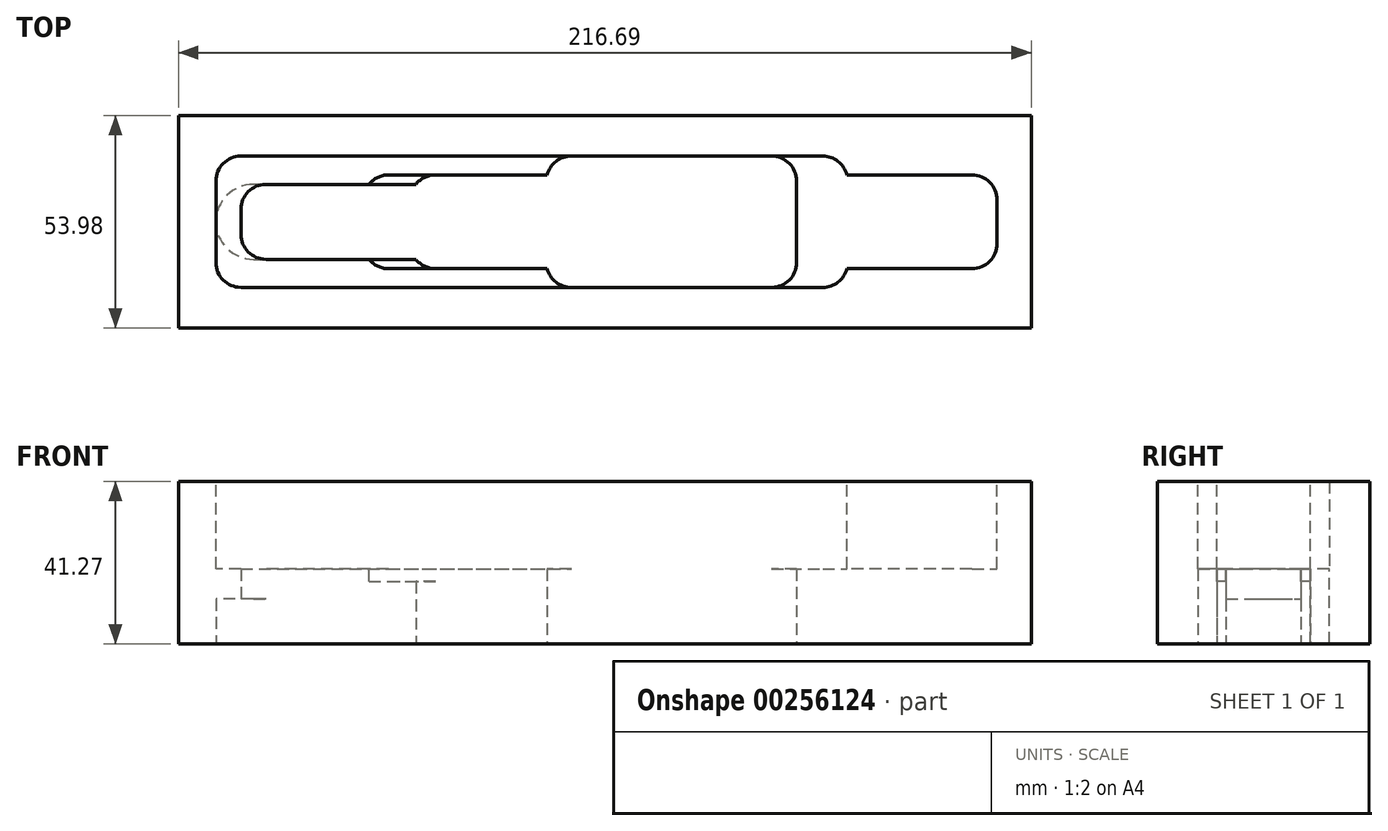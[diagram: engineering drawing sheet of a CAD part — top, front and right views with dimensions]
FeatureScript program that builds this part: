
annotation { "Feature Type Name" : "Feature", "Feature Type Description" : "" }
export const myFeature = defineFeature(function(context is Context, id is Id, definition is map)
    precondition{}
    {
        {
            var Q0;
            Q0=qCreatedBy(makeId("Top.planeOp"),FACE);
            var sketch = newSketch(context, id + "F0", { "sketchPlane" : qUnion([Q0])});
            skLineSegment(sketch, "E0.bottom", {"start": v(127, 26.99) * mm, "end": v(-127, 26.99) * mm});
            skLineSegment(sketch, "E0.top", {"start": v(127, -26.99) * mm, "end": v(-127, -26.99) * mm});
            skLineSegment(sketch, "E0.left", {"start": v(127, 26.99) * mm, "end": v(127, -26.99) * mm});
            skLineSegment(sketch, "E0.right", {"start": v(-127, 26.99) * mm, "end": v(-127, -26.99) * mm});
            skPoint(sketch, "E0.middle", {"position": v(0, 0) * mm});
            skSolve(sketch);
        }
        {
            var Q0;
            Q0 = qSketchRegion(id + "F0", true);
            extrude(context, id + "F1", {"entities" : qUnion([Q0]), "depth" : 41.27 * mm});
        }
        {
            var Q0;
            Q0=makeQuery(id+"F1.opExtrude","CAP_FACE",FACE,{"disambiguationData":[OSD([sQuery(id+"F0.wireOp",EDGE,"E0.bottom"),sQuery(id+"F0.wireOp",EDGE,"E0.top"),sQuery(id+"F0.wireOp",EDGE,"E0.left"),sQuery(id+"F0.wireOp",EDGE,"E0.right")])],"isStart":false});
            var sketch = newSketch(context, id + "F2", { "sketchPlane" : qUnion([Q0])});
            skLineSegment(sketch, "E1.bottom", {"start": v(-80.17, -16.67) * mm, "end": v(80.17, -16.67) * mm});
            skLineSegment(sketch, "E1.top", {"start": v(-80.17, 16.67) * mm, "end": v(80.17, 16.67) * mm});
            skLineSegment(sketch, "E1.left", {"start": v(-80.17, -16.67) * mm, "end": v(-80.17, 16.67) * mm});
            skPoint(sketch, "E1.middle", {"position": v(0, 0) * mm});
            skLineSegment(sketch, "E2", {"start": v(80.17, 16.67) * mm, "end": v(80.17, 11.9) * mm});
            skLineSegment(sketch, "E3", {"start": v(80.17, 11.9) * mm, "end": v(118.27, 11.9) * mm});
            skLineSegment(sketch, "E4", {"start": v(118.27, 11.9) * mm, "end": v(118.27, -11.9) * mm});
            skLineSegment(sketch, "E5", {"start": v(118.27, -11.9) * mm, "end": v(80.17, -11.9) * mm});
            skLineSegment(sketch, "E6", {"start": v(80.17, -11.9) * mm, "end": v(80.17, -16.67) * mm});
            skSolve(sketch);
        }
        {
            var Q0;
            Q0 = qSketchRegion(id + "F2", true);
            extrude(context, id + "F3", {"entities" : qUnion([Q0]), "operationType" : NewBodyOperationType.REMOVE, "oppositeDirection" : true, "depth" : 22.22 * mm});
        }
        {
            var Q0;
            Q0=makeQuery(id+"F3.boolean.opBoolean","COPY",EDGE,{"derivedFrom":makeQuery(id+"F3.opExtrude","SWEPT_EDGE",EDGE,{"disambiguationData":[OSD([sQuery(id+"F2.wireOp",EDGE,"E1.bottom"),sQuery(id+"F2.wireOp",EDGE,"E1.left")])]})});
            var Q1;
            Q1=makeQuery(id+"F3.boolean.opBoolean","COPY",EDGE,{"derivedFrom":makeQuery(id+"F3.opExtrude","SWEPT_EDGE",EDGE,{"disambiguationData":[OSD([sQuery(id+"F2.wireOp",EDGE,"E4"),sQuery(id+"F2.wireOp",EDGE,"E5")])]})});
            var Q2;
            Q2=makeQuery(id+"F3.boolean.opBoolean","COPY",EDGE,{"derivedFrom":makeQuery(id+"F3.opExtrude","SWEPT_EDGE",EDGE,{"disambiguationData":[OSD([sQuery(id+"F2.wireOp",EDGE,"E3"),sQuery(id+"F2.wireOp",EDGE,"E4")])]})});
            var Q3;
            Q3=makeQuery(id+"F3.boolean.opBoolean","COPY",EDGE,{"derivedFrom":makeQuery(id+"F3.opExtrude","SWEPT_EDGE",EDGE,{"disambiguationData":[OSD([sQuery(id+"F2.wireOp",EDGE,"E1.top"),sQuery(id+"F2.wireOp",EDGE,"E2")])]})});
            var Q4;
            Q4=makeQuery(id+"F3.boolean.opBoolean","COPY",EDGE,{"derivedFrom":makeQuery(id+"F3.opExtrude","SWEPT_EDGE",EDGE,{"disambiguationData":[OSD([sQuery(id+"F2.wireOp",EDGE,"E1.top"),sQuery(id+"F2.wireOp",EDGE,"E1.left")])]})});
            var Q5;
            Q5=makeQuery(id+"F3.boolean.opBoolean","COPY",EDGE,{"derivedFrom":makeQuery(id+"F3.opExtrude","SWEPT_EDGE",EDGE,{"disambiguationData":[OSD([sQuery(id+"F2.wireOp",EDGE,"E1.bottom"),sQuery(id+"F2.wireOp",EDGE,"E6")])]})});
            fillet(context, id + "F4", {"entities" : qUnion([Q0, Q1, Q2, Q3, Q4, Q5]), "radius" : 6.35 * mm, "tangentPropagation" : true, "allowEdgeOverflow" : false});
        }
        {
            var Q0;
            Q0=makeQuery(id+"F1.opExtrude","CAP_FACE",FACE,{"disambiguationData":[OSD([sQuery(id+"F0.wireOp",EDGE,"E0.bottom"),sQuery(id+"F0.wireOp",EDGE,"E0.top"),sQuery(id+"F0.wireOp",EDGE,"E0.left"),sQuery(id+"F0.wireOp",EDGE,"E0.right")])],"isStart":true});
            var sketch = newSketch(context, id + "F5", { "sketchPlane" : qUnion([Q0])});
            skLineSegment(sketch, "E7", {"start": v(-70.64, 9.52) * mm, "end": v(-29.37, 9.52) * mm});
            skLineSegment(sketch, "E8", {"start": v(-29.37, 9.52) * mm, "end": v(-29.37, 11.9) * mm});
            skLineSegment(sketch, "E9", {"start": v(-29.37, 11.9) * mm, "end": v(3.97, 11.9) * mm});
            skLineSegment(sketch, "E10", {"start": v(3.97, 11.9) * mm, "end": v(3.97, 16.67) * mm});
            skLineSegment(sketch, "E11", {"start": v(3.97, 16.67) * mm, "end": v(67.39, 16.67) * mm});
            skLineSegment(sketch, "E12", {"start": v(67.39, 16.67) * mm, "end": v(67.39, -16.67) * mm});
            skLineSegment(sketch, "E13", {"start": v(67.39, -16.67) * mm, "end": v(3.97, -16.67) * mm});
            skLineSegment(sketch, "E14", {"start": v(3.97, -16.67) * mm, "end": v(3.97, -11.9) * mm});
            skLineSegment(sketch, "E15", {"start": v(3.97, -11.9) * mm, "end": v(-29.37, -11.9) * mm});
            skLineSegment(sketch, "E16", {"start": v(-29.37, -11.9) * mm, "end": v(-29.37, -9.53) * mm});
            skLineSegment(sketch, "E17", {"start": v(-29.37, -9.53) * mm, "end": v(-70.64, -9.53) * mm});
            skArc(sketch, "E18", {"start": v(-70.64, 9.52) * mm, "mid": v(-80.17, 0) * mm, "end": v(-70.64, -9.53) * mm});
            skSolve(sketch);
        }
        {
            var Q0;
            Q0 = qSketchRegion(id + "F5", true);
            extrude(context, id + "F6", {"entities" : qUnion([Q0]), "operationType" : NewBodyOperationType.REMOVE, "oppositeDirection" : true, "depth" : 11.43 * mm});
        }
        {
            var Q0;
            Q0=makeQuery(id+"F1.opExtrude","CAP_FACE",FACE,{"disambiguationData":[OSD([sQuery(id+"F0.wireOp",EDGE,"E0.bottom"),sQuery(id+"F0.wireOp",EDGE,"E0.top"),sQuery(id+"F0.wireOp",EDGE,"E0.left"),sQuery(id+"F0.wireOp",EDGE,"E0.right")])],"isStart":true});
            var sketch = newSketch(context, id + "F7", { "sketchPlane" : qUnion([Q0])});
            skLineSegment(sketch, "E19", {"start": v(-70.64, 9.52) * mm, "end": v(-29.37, 9.52) * mm});
            skLineSegment(sketch, "E20", {"start": v(-29.37, 9.52) * mm, "end": v(-29.37, 11.9) * mm});
            skLineSegment(sketch, "E21", {"start": v(-29.37, 11.9) * mm, "end": v(3.97, 11.9) * mm});
            skLineSegment(sketch, "E22", {"start": v(3.97, 11.9) * mm, "end": v(3.97, 16.67) * mm});
            skLineSegment(sketch, "E23", {"start": v(3.97, 16.67) * mm, "end": v(67.39, 16.67) * mm});
            skLineSegment(sketch, "E24", {"start": v(67.39, 16.67) * mm, "end": v(67.39, -16.67) * mm});
            skLineSegment(sketch, "E25", {"start": v(67.39, -16.67) * mm, "end": v(3.97, -16.67) * mm});
            skLineSegment(sketch, "E26", {"start": v(3.97, -16.67) * mm, "end": v(3.97, -11.9) * mm});
            skLineSegment(sketch, "E27", {"start": v(3.97, -11.9) * mm, "end": v(-29.37, -11.9) * mm});
            skLineSegment(sketch, "E28", {"start": v(-29.37, -11.9) * mm, "end": v(-29.37, -9.53) * mm});
            skLineSegment(sketch, "E29", {"start": v(-29.37, -9.53) * mm, "end": v(-70.64, -9.53) * mm});
            skArc(sketch, "E30", {"start": v(-70.64, 9.52) * mm, "mid": v(-72.25, 9.39) * mm, "end": v(-73.82, 8.98) * mm});
            skArc(sketch, "E31", {"start": v(-70.64, -9.53) * mm, "mid": v(-72.25, -9.39) * mm, "end": v(-73.82, -8.98) * mm});
            skLineSegment(sketch, "E32", {"start": v(-73.82, 8.98) * mm, "end": v(-73.82, -8.98) * mm});
            skSolve(sketch);
        }
        {
            var Q0;
            Q0 = qSketchRegion(id + "F7", true);
            extrude(context, id + "F8", {"entities" : qUnion([Q0]), "operationType" : NewBodyOperationType.REMOVE, "endBound" : BoundingType.THROUGH_ALL, "oppositeDirection" : true, "depth" : 25.4 * mm});
        }
        {
            var Q0;
            Q0=makeQuery(id+"F8.boolean.opBoolean","MERGE",EDGE,{"derivedFrom":[makeQuery(id+"F6.boolean.opBoolean","COPY",EDGE,{"derivedFrom":makeQuery(id+"F6.opExtrude","SWEPT_EDGE",EDGE,{"disambiguationData":[OSD([sQuery(id+"F5.wireOp",EDGE,"E10"),sQuery(id+"F5.wireOp",EDGE,"E11")])]})}),makeQuery(id+"F8.opExtrude","SWEPT_EDGE",EDGE,{"disambiguationData":[OSD([sQuery(id+"F7.wireOp",EDGE,"E22"),sQuery(id+"F7.wireOp",EDGE,"E23")])]})]});
            var Q1;
            Q1=makeQuery(id+"F8.boolean.opBoolean","MERGE",EDGE,{"derivedFrom":[makeQuery(id+"F6.boolean.opBoolean","COPY",EDGE,{"derivedFrom":makeQuery(id+"F6.opExtrude","SWEPT_EDGE",EDGE,{"disambiguationData":[OSD([sQuery(id+"F5.wireOp",EDGE,"E8"),sQuery(id+"F5.wireOp",EDGE,"E9")])]})}),makeQuery(id+"F8.opExtrude","SWEPT_EDGE",EDGE,{"disambiguationData":[OSD([sQuery(id+"F7.wireOp",EDGE,"E20"),sQuery(id+"F7.wireOp",EDGE,"E21")])]})]});
            var Q2;
            Q2=makeQuery(id+"F8.boolean.opBoolean","MERGE",EDGE,{"derivedFrom":[makeQuery(id+"F6.boolean.opBoolean","COPY",EDGE,{"derivedFrom":makeQuery(id+"F6.opExtrude","SWEPT_EDGE",EDGE,{"disambiguationData":[OSD([sQuery(id+"F5.wireOp",EDGE,"E11"),sQuery(id+"F5.wireOp",EDGE,"E12")])]})}),makeQuery(id+"F8.opExtrude","SWEPT_EDGE",EDGE,{"disambiguationData":[OSD([sQuery(id+"F7.wireOp",EDGE,"E23"),sQuery(id+"F7.wireOp",EDGE,"E24")])]})]});
            var Q3;
            Q3=makeQuery(id+"F8.boolean.opBoolean","MERGE",EDGE,{"derivedFrom":[makeQuery(id+"F6.boolean.opBoolean","COPY",EDGE,{"derivedFrom":makeQuery(id+"F6.opExtrude","SWEPT_EDGE",EDGE,{"disambiguationData":[OSD([sQuery(id+"F5.wireOp",EDGE,"E12"),sQuery(id+"F5.wireOp",EDGE,"E13")])]})}),makeQuery(id+"F8.opExtrude","SWEPT_EDGE",EDGE,{"disambiguationData":[OSD([sQuery(id+"F7.wireOp",EDGE,"E24"),sQuery(id+"F7.wireOp",EDGE,"E25")])]})]});
            var Q4;
            Q4=makeQuery(id+"F8.boolean.opBoolean","MERGE",EDGE,{"derivedFrom":[makeQuery(id+"F6.boolean.opBoolean","COPY",EDGE,{"derivedFrom":makeQuery(id+"F6.opExtrude","SWEPT_EDGE",EDGE,{"disambiguationData":[OSD([sQuery(id+"F5.wireOp",EDGE,"E13"),sQuery(id+"F5.wireOp",EDGE,"E14")])]})}),makeQuery(id+"F8.opExtrude","SWEPT_EDGE",EDGE,{"disambiguationData":[OSD([sQuery(id+"F7.wireOp",EDGE,"E25"),sQuery(id+"F7.wireOp",EDGE,"E26")])]})]});
            var Q5;
            Q5=makeQuery(id+"F8.boolean.opBoolean","MERGE",EDGE,{"derivedFrom":[makeQuery(id+"F6.boolean.opBoolean","COPY",EDGE,{"derivedFrom":makeQuery(id+"F6.opExtrude","SWEPT_EDGE",EDGE,{"disambiguationData":[OSD([sQuery(id+"F5.wireOp",EDGE,"E15"),sQuery(id+"F5.wireOp",EDGE,"E16")])]})}),makeQuery(id+"F8.opExtrude","SWEPT_EDGE",EDGE,{"disambiguationData":[OSD([sQuery(id+"F7.wireOp",EDGE,"E27"),sQuery(id+"F7.wireOp",EDGE,"E28")])]})]});
            var Q6;
            Q6=makeQuery(id+"F8.boolean.opBoolean","COPY",EDGE,{"derivedFrom":makeQuery(id+"F8.opExtrude","SWEPT_EDGE",EDGE,{"disambiguationData":[OSD([sQuery(id+"F5.wireOp",EDGE,"E18"),sQuery(id+"F7.wireOp",EDGE,"E31"),sQuery(id+"F7.wireOp",EDGE,"E32")])]})});
            var Q7;
            Q7=makeQuery(id+"F8.boolean.opBoolean","COPY",EDGE,{"derivedFrom":makeQuery(id+"F8.opExtrude","SWEPT_EDGE",EDGE,{"disambiguationData":[OSD([sQuery(id+"F5.wireOp",EDGE,"E18"),sQuery(id+"F7.wireOp",EDGE,"E30"),sQuery(id+"F7.wireOp",EDGE,"E32")])]})});
            fillet(context, id + "F9", {"entities" : qUnion([Q0, Q1, Q2, Q3, Q4, Q5, Q6, Q7]), "radius" : 6.35 * mm, "tangentPropagation" : true, "allowEdgeOverflow" : false});
        }
        {
            var Q0;
            Q0=makeQuery(id+"F1.opExtrude","SWEPT_FACE",FACE,{"disambiguationData":[OSD([sQuery(id+"F0.wireOp",EDGE,"E0.top")])]});
            var sketch = newSketch(context, id + "F10", { "sketchPlane" : qUnion([Q0])});
            skLineSegment(sketch, "E33.bottom", {"start": v(-127, 41.28) * mm, "end": v(-89.7, 41.28) * mm});
            skLineSegment(sketch, "E33.top", {"start": v(-127, 0) * mm, "end": v(-89.7, 0) * mm});
            skLineSegment(sketch, "E33.left", {"start": v(-127, 41.28) * mm, "end": v(-127, 0) * mm});
            skLineSegment(sketch, "E33.right", {"start": v(-89.7, 41.28) * mm, "end": v(-89.7, 0) * mm});
            skSolve(sketch);
        }
        {
            var Q0;
            Q0 = qSketchRegion(id + "F10", true);
            extrude(context, id + "F11", {"entities" : qUnion([Q0]), "operationType" : NewBodyOperationType.REMOVE, "endBound" : BoundingType.THROUGH_ALL, "oppositeDirection" : true, "depth" : 25.4 * mm});
        }
        {
            var Q0;
            {var subQ0=sQuery(id+"F2.wireOp",EDGE,"E1.bottom");var subQ1=sQuery(id+"F2.wireOp",EDGE,"E1.left");var subQ2=sQuery(id+"F2.wireOp",EDGE,"E1.top");Q0=makeQuery(id+"F8.boolean.opBoolean","SPLIT",FACE,{"disambiguationData":[TD([makeQuery(id+"F3.boolean.opBoolean","COPY",FACE,{"derivedFrom":makeQuery(id+"F3.opExtrude","SWEPT_FACE",FACE,{"disambiguationData":[OSD([subQ1])]})})])],"derivedFrom":makeQuery(id+"F3.boolean.opBoolean","COPY",FACE,{"derivedFrom":makeQuery(id+"F3.opExtrude","CAP_FACE",FACE,{"disambiguationData":[OSD([subQ0,subQ2,subQ1,sQuery(id+"F2.wireOp",EDGE,"E2"),sQuery(id+"F2.wireOp",EDGE,"E3"),sQuery(id+"F2.wireOp",EDGE,"E4"),sQuery(id+"F2.wireOp",EDGE,"E5"),sQuery(id+"F2.wireOp",EDGE,"E6")])],"isStart":false})})});}
            var sketch = newSketch(context, id + "F12", { "sketchPlane" : qUnion([Q0])});
            skLineSegment(sketch, "E34.bottom", {"start": v(-41.28, 9.53) * mm, "end": v(-22.23, 9.53) * mm});
            skLineSegment(sketch, "E34.top", {"start": v(-41.28, 11.9) * mm, "end": v(-22.23, 11.9) * mm});
            skLineSegment(sketch, "E34.left", {"start": v(-41.28, 9.53) * mm, "end": v(-41.28, 11.9) * mm});
            skLineSegment(sketch, "E34.right", {"start": v(-22.23, 9.53) * mm, "end": v(-22.23, 11.9) * mm});
            skLineSegment(sketch, "E35.MirrorCS", {"start": v(-41.28, -9.53) * mm, "end": v(-22.23, -9.53) * mm});
            skLineSegment(sketch, "E36.MirrorCS", {"start": v(-41.28, -11.9) * mm, "end": v(-22.23, -11.9) * mm});
            skLineSegment(sketch, "E37.MirrorCS", {"start": v(-41.28, -9.53) * mm, "end": v(-41.28, -11.9) * mm});
            skLineSegment(sketch, "E38.MirrorCS", {"start": v(-22.23, -9.53) * mm, "end": v(-22.23, -11.9) * mm});
            skSolve(sketch);
        }
        {
            var Q0;
            Q0 = qSketchRegion(id + "F12", true);
            extrude(context, id + "F13", {"entities" : qUnion([Q0]), "operationType" : NewBodyOperationType.REMOVE, "oppositeDirection" : true, "depth" : 3.17 * mm});
        }
        {
            var Q0;
            Q0=makeQuery(id+"F13.boolean.opBoolean","COPY",EDGE,{"derivedFrom":makeQuery(id+"F13.opExtrude","SWEPT_EDGE",EDGE,{"disambiguationData":[OSD([sQuery(id+"F12.wireOp",EDGE,"E34.top"),sQuery(id+"F12.wireOp",EDGE,"E34.left")])]})});
            var Q1;
            Q1=makeQuery(id+"F13.boolean.opBoolean","COPY",EDGE,{"derivedFrom":makeQuery(id+"F13.opExtrude","SWEPT_EDGE",EDGE,{"disambiguationData":[OSD([sQuery(id+"F12.wireOp",EDGE,"E36.MirrorCS"),sQuery(id+"F12.wireOp",EDGE,"E37.MirrorCS")])]})});
            fillet(context, id + "F14", {"entities" : qUnion([Q0, Q1]), "radius" : 6.35 * mm, "tangentPropagation" : true, "allowEdgeOverflow" : false});
        }
    });
